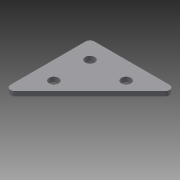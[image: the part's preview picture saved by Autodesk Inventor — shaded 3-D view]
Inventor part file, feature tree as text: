
AUTODESK INVENTOR PART (.ipt)
format: ipt  version: 2013 (Build 170138000, 138)  size: 86,528 bytes
history: native  units: in
note: dims shown in document units (in); Inventor stores cm internally (conversion verified against a paired STEP export)
features: extrude x1, sketch x1
ambient origin geometry x8: Origin, YZ Plane, XZ Plane, XY Plane, X Axis, Y Axis, Z Axis, Center Point
bodies: Solid1 (feature_tree)
feature tree (2):
  extrude  "Extrusion1"  Depth=0.266in
  sketch  "Sketch1"  dims[d3=0.266in d4=0.266in d5=0.266in d6=0.5in d7=0.5in d8=0.5in d9=1.0in d10=1.0in d11=0.5in d12=2.5in d13=2.5in d14=0.125in d15=0.125in d16=0.0in]
